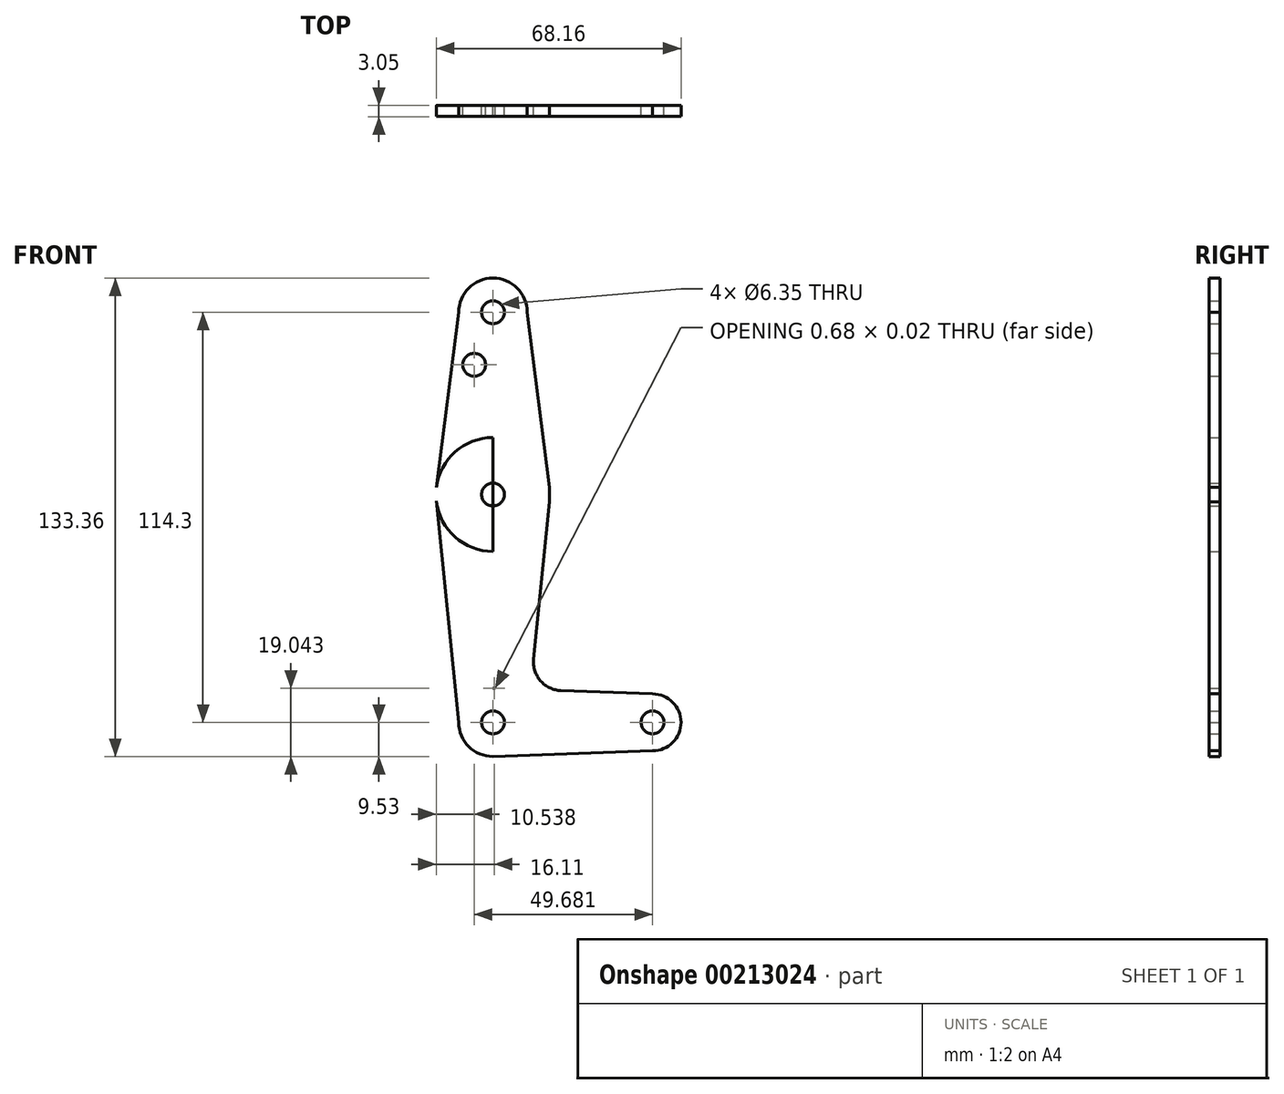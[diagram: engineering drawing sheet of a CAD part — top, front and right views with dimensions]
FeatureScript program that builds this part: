
annotation { "Feature Type Name" : "Feature", "Feature Type Description" : "" }
export const myFeature = defineFeature(function(context is Context, id is Id, definition is map)
    precondition{}
    {
        {
            var Q0;
            Q0=qCreatedBy(makeId("Front.planeOp"),FACE);
            var sketch = newSketch(context, id + "F0", { "sketchPlane" : qUnion([Q0])});
            skLineSegment(sketch, "E0", {"start": v(0, 0) * mm, "end": v(0, 114.3) * mm});
            skLineSegment(sketch, "E1", {"start": v(0, 0) * mm, "end": v(0, 63.5) * mm});
            skLineSegment(sketch, "E2", {"start": v(0, 0) * mm, "end": v(44.45, 0) * mm});
            skCircle(sketch, "E3", {"center": v(0, 114.3) * mm, "radius": 9.53 * mm});
            skCircle(sketch, "E4", {"center": v(0, 63.5) * mm, "radius": 15.88 * mm});
            skCircle(sketch, "E5", {"center": v(0, 0) * mm, "radius": 9.53 * mm});
            skCircle(sketch, "E6", {"center": v(44.45, 0) * mm, "radius": 7.94 * mm});
            skLineSegment(sketch, "E7", {"start": v(9.53, 114.3) * mm, "end": v(15.75, 65.5) * mm});
            skLineSegment(sketch, "E8", {"start": v(15.75, 65.5) * mm, "end": v(15.75, 61.5) * mm});
            skLineSegment(sketch, "E9", {"start": v(15.75, 61.5) * mm, "end": v(11.34, 17.59) * mm});
            skLineSegment(sketch, "E10", {"start": v(18.97, 8.85) * mm, "end": v(44.45, 7.94) * mm});
            skLineSegment(sketch, "E11", {"start": v(0, -9.52) * mm, "end": v(44.45, -7.94) * mm});
            skCircle(sketch, "E12", {"center": v(0, 114.3) * mm, "radius": 3.18 * mm});
            skCircle(sketch, "E13", {"center": v(0, 63.5) * mm, "radius": 3.18 * mm});
            skCircle(sketch, "E14", {"center": v(0, 0) * mm, "radius": 3.18 * mm});
            skCircle(sketch, "E15", {"center": v(44.45, 0) * mm, "radius": 3.18 * mm});
            skLineSegment(sketch, "E16", {"start": v(-15.75, 65.5) * mm, "end": v(-9.53, 114.3) * mm});
            skCircle(sketch, "E17", {"center": v(-5.23, 99.65) * mm, "radius": 3.18 * mm});
            skLineSegment(sketch, "E18", {"start": v(-15.77, 61.7) * mm, "end": v(-9.57, 0) * mm});
            skLineSegment(sketch, "E19", {"start": v(0, 0) * mm, "end": v(-9.57, 0) * mm});
            skArc(sketch, "E20.filletArc", {"start": v(11.34, 17.59) * mm, "mid": v(13.26, 11.57) * mm, "end": v(18.97, 8.85) * mm});
            skLineSegment(sketch, "E21", {"start": v(0, 9.52) * mm, "end": v(44.45, 7.94) * mm});
            skSolve(sketch);
        }
        {
            var Q0;
            Q0=makeQuery(id+"F0.imprint","IMPRINT",FACE,{"disambiguationData":[TD([[makeQuery(id+"F0.imprint","IMPRINT",EDGE,{"derivedFrom":sQuery(id+"F0.wireOp",EDGE,"E12")}),-1.0]])]});
            var Q1;
            {var subQ5=sQuery(id+"F0.wireOp",EDGE,"E7");Q1=makeQuery(id+"F0.imprint","IMPRINT",FACE,{"disambiguationData":[TD([[makeQuery(id+"F0.imprint","IMPRINT",EDGE,{"derivedFrom":subQ5}),-1.0]])]});}
            var Q2;
            {var subQ0=sQuery(id+"F0.wireOp",EDGE,"E16");Q2=makeQuery(id+"F0.imprint","IMPRINT",FACE,{"disambiguationData":[TD([[makeQuery(id+"F0.imprint","IMPRINT",EDGE,{"derivedFrom":subQ0}),-1.0]])]});}
            var Q3;
            {var subQ0=sQuery(id+"F0.wireOp",EDGE,"E8");Q3=makeQuery(id+"F0.imprint","IMPRINT",FACE,{"disambiguationData":[TD([[makeQuery(id+"F0.imprint","IMPRINT",EDGE,{"derivedFrom":subQ0}),-1.0]])]});}
            var Q4;
            {var subQ2=sQuery(id+"F0.wireOp",EDGE,"E0");var subQ6=sQuery(id+"F0.wireOp",EDGE,"E13");var subQ9=makeQuery(id+"F0.imprint","INTERSECT",VERTEX,{"derivedFrom":[subQ2,subQ6]});Q4=makeQuery(id+"F0.imprint","IMPRINT",FACE,{"disambiguationData":[TD([[makeQuery(id+"F0.imprint","IMPRINT",EDGE,{"disambiguationData":[TD([[subQ9,-1.0]])],"derivedFrom":subQ2}),1.0]])]});}
            var Q5;
            {var subQ0=sQuery(id+"F0.wireOp",EDGE,"E18");Q5=makeQuery(id+"F0.imprint","IMPRINT",FACE,{"disambiguationData":[TD([[makeQuery(id+"F0.imprint","IMPRINT",EDGE,{"derivedFrom":subQ0}),1.0]])]});}
            var Q6;
            {var subQ0=sQuery(id+"F0.wireOp",EDGE,"E9");Q6=makeQuery(id+"F0.imprint","IMPRINT",FACE,{"disambiguationData":[TD([[makeQuery(id+"F0.imprint","IMPRINT",EDGE,{"derivedFrom":subQ0}),-1.0]])]});}
            var Q7;
            {var subQ0=sQuery(id+"F0.wireOp",EDGE,"E14");var subQ1=sQuery(id+"F0.wireOp",EDGE,"E2");var subQ2=makeQuery(id+"F0.imprint","INTERSECT",VERTEX,{"derivedFrom":[subQ1,subQ0]});Q7=makeQuery(id+"F0.imprint","IMPRINT",FACE,{"disambiguationData":[TD([[makeQuery(id+"F0.imprint","IMPRINT",EDGE,{"disambiguationData":[TD([[subQ2,-1.0]])],"derivedFrom":subQ1}),1.0]])]});}
            var Q8;
            {var subQ6=sQuery(id+"F0.wireOp",EDGE,"E14");var subQ7=sQuery(id+"F0.wireOp",EDGE,"E2");var subQ8=makeQuery(id+"F0.imprint","INTERSECT",VERTEX,{"derivedFrom":[subQ7,subQ6]});Q8=makeQuery(id+"F0.imprint","IMPRINT",FACE,{"disambiguationData":[TD([[makeQuery(id+"F0.imprint","IMPRINT",EDGE,{"disambiguationData":[TD([[subQ8,-1.0]])],"derivedFrom":subQ7}),-1.0]])]});}
            var Q9;
            {var subQ1=sQuery(id+"F0.wireOp",EDGE,"E1");var subQ3=sQuery(id+"F0.wireOp",EDGE,"E14");var subQ4=makeQuery(id+"F0.imprint","INTERSECT",VERTEX,{"derivedFrom":[subQ1,subQ3]});Q9=makeQuery(id+"F0.imprint","IMPRINT",FACE,{"disambiguationData":[TD([[makeQuery(id+"F0.imprint","IMPRINT",EDGE,{"disambiguationData":[TD([[subQ4,-1.0]])],"derivedFrom":subQ3}),-1.0]])]});}
            var Q10;
            {var subQ4=sQuery(id+"F0.wireOp",EDGE,"E6");var subQ6=sQuery(id+"F0.wireOp",EDGE,"E2");var subQ7=makeQuery(id+"F0.imprint","INTERSECT",VERTEX,{"derivedFrom":[subQ6,subQ4]});Q10=makeQuery(id+"F0.imprint","IMPRINT",FACE,{"disambiguationData":[TD([[makeQuery(id+"F0.imprint","IMPRINT",EDGE,{"disambiguationData":[TD([[subQ7,1.0]])],"derivedFrom":subQ6}),1.0]])]});}
            var Q11;
            {var subQ0=sQuery(id+"F0.wireOp",EDGE,"E6");var subQ1=sQuery(id+"F0.wireOp",EDGE,"E2");var subQ2=makeQuery(id+"F0.imprint","INTERSECT",VERTEX,{"derivedFrom":[subQ1,subQ0]});Q11=makeQuery(id+"F0.imprint","IMPRINT",FACE,{"disambiguationData":[TD([[makeQuery(id+"F0.imprint","IMPRINT",EDGE,{"disambiguationData":[TD([[subQ2,1.0]])],"derivedFrom":subQ1}),-1.0]])]});}
            var Q12;
            Q12=makeQuery(id+"F0.imprint","IMPRINT",FACE,{"disambiguationData":[TD([[makeQuery(id+"F0.imprint","IMPRINT",EDGE,{"derivedFrom":sQuery(id+"F0.wireOp",EDGE,"E15")}),-1.0]])]});
            extrude(context, id + "F1", {"entities" : qUnion([Q0, Q1, Q2, Q3, Q4, Q5, Q6, Q7, Q8, Q9, Q10, Q11, Q12]), "depth" : 3.05 * mm});
        }
    });
